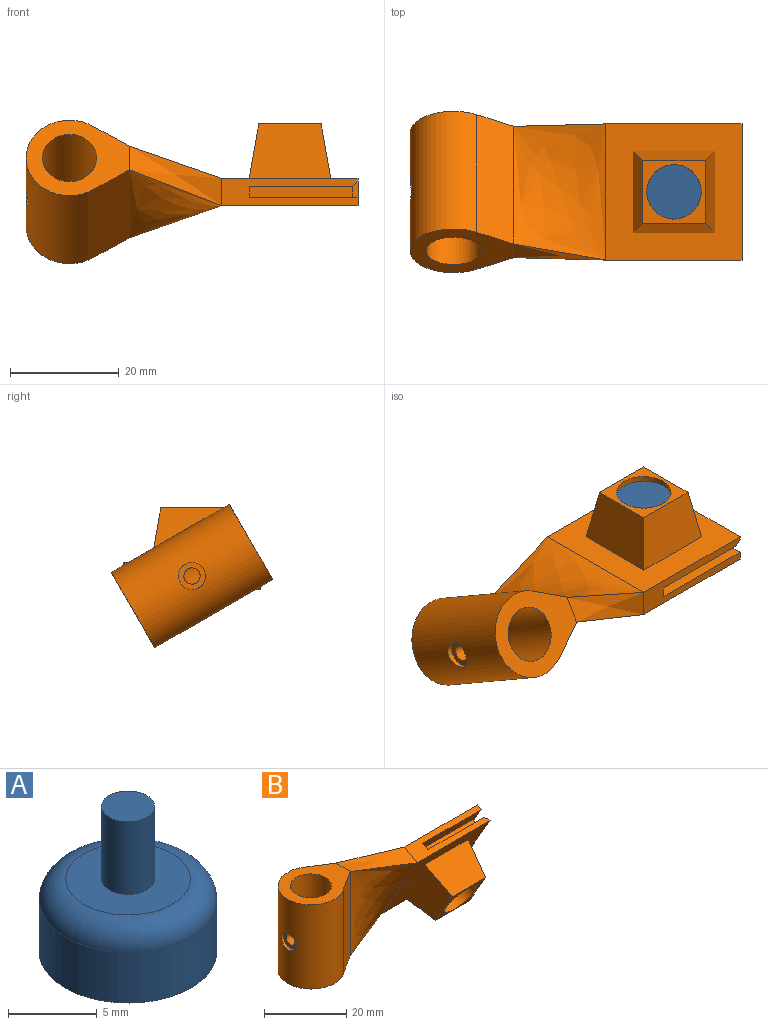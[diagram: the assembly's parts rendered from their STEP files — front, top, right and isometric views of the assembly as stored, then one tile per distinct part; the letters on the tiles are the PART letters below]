
ASSEMBLY  parts=2 mates=1
PART A: 6 faces, bbox 10.8x10.8x10 mm
  f0: cylinder r=5mm len=10mm, axis (0,0,-1), area 110mm2, adj f2,f3
  f1: plane 7x7mm, normal (0,0,1), area 31.4mm2, adj f3,f4
  f2: plane 10x10mm, normal (0,0,-1), area 78.5mm2, adj f0
  f3: torus R=3.5mm, axis (0,0,1), area 66mm2, adj f0,f1
  f4: cylinder r=1.5mm len=5mm, axis (0,0,-1), area 47.1mm2, adj f1,f5
  f5: plane 3x3mm, normal (0,0,1), area 7.1mm2, adj f4
PART B: 38 faces, bbox 61x22.1x25 mm
  f0: plane 24.15x16.83mm, normal (1,0,0), area 95mm2, adj f14,f15,f16,f17,f25,f28,f31,f32
  f1: cylinder r=8mm len=25mm, axis (0,0,-1), area 834.4mm2, adj f3,f4,f5,f6,f8
  f2: cylinder r=5mm len=25mm, axis (0,0,-1), area 778.2mm2, adj f5,f6,f7
  f3: plane 25x6.72mm, normal (0.54,0.84,0), area 198.8mm2, adj f1,f5,f6,f10
  f4: plane 25x6.72mm, normal (0.54,-0.84,0), area 198.8mm2, adj f1,f5,f6,f12
  f5: plane 19x16mm, normal (0,0,1), area 149.3mm2, adj f1,f2,f3,f4,f11
  f6: plane 19x16mm, normal (0,0,-1), area 149.3mm2, adj f1,f2,f3,f4,f13
  f7: cylinder r=1.5mm len=3mm, axis (-1,0,0), area 19.9mm2, adj f2,f9
  f8: cylinder r=2.5mm len=5mm, axis (-1,0,0), area 12.6mm2, adj f1,f9
  f9: plane 5x5mm, normal (-1,0,0), area 12.6mm2, adj f7,f8
  f10: bspline ~25x17mm, area 425mm2, adj f3,f11,f13,f15
  f11: bspline ~17x10.92mm, area 83.3mm2, adj f5,f10,f12,f16
  f12: bspline ~25x17mm, area 425mm2, adj f4,f11,f13,f17
  f13: bspline ~17x10.92mm, area 83.3mm2, adj f6,f10,f12,f14
  f14: plane 25x4.33mm, normal (0,0.5,-0.87), area 84.5mm2, adj f0,f13,f15,f17,f27,f28,f30,f33
  f15: plane 25x21.65mm, normal (0,0.87,0.5), area 617.9mm2, adj f0,f10,f14,f16,f37
  f16: plane 25x4.33mm, normal (0,-0.5,0.87), area 84.5mm2, adj f0,f11,f15,f17,f23,f25,f26,f32
  f17: plane 25x21.65mm, normal (0,-0.87,-0.5), area 400mm2, adj f0,f12,f14,f16,f18,f19,f20,f21
  f18: plane 16.46x15.28mm, normal (0.98,-0.15,-0.09), area 134.4mm2, adj f17,f19,f21,f22
  f19: plane 15x7.78mm, normal (0,-0.64,0.77), area 134.4mm2, adj f17,f18,f20,f22
  f20: plane 16.46x15.28mm, normal (-0.98,-0.15,-0.09), area 134.4mm2, adj f17,f19,f21,f22
  f21: plane 15x9.54mm, normal (0,0.34,-0.94), area 134.4mm2, adj f17,f18,f20,f22
  f22: plane 11.47x9.94mm, normal (0,-0.87,-0.5), area 53.1mm2, adj f18,f19,f20,f21,f35
  f23: plane 19x3.46mm, normal (0,0.87,0.5), area 76mm2, adj f16,f24,f26,f32
  f24: plane 19x1.73mm, normal (0,-0.5,0.87), area 38mm2, adj f23,f25,f26,f31
  f25: plane 20x4.33mm, normal (0,-0.87,-0.5), area 80.5mm2, adj f0,f16,f24,f26,f31
  f26: plane 4.46x3.73mm, normal (1,0,0), area 8mm2, adj f16,f23,f24,f25
  f27: plane 19x3.46mm, normal (0,0.87,0.5), area 76mm2, adj f14,f29,f30,f33
  f28: plane 20x4.33mm, normal (0,-0.87,-0.5), area 80.5mm2, adj f0,f14,f29,f30,f34
  f29: plane 19x1.73mm, normal (0,0.5,-0.87), area 38mm2, adj f27,f28,f30,f34
  f30: plane 4.46x3.73mm, normal (1,0,0), area 8mm2, adj f14,f27,f28,f29
  f31: plane 2.6x2.37mm, normal (0.71,-0.35,0.61), area 3.5mm2, adj f0,f24,f25,f32
  f32: plane 4.83x2.87mm, normal (0.71,0.61,0.35), area 6.4mm2, adj f0,f16,f23,f31
  f33: plane 4.33x3.37mm, normal (0.71,0.61,0.35), area 6.4mm2, adj f0,f14,f27,f34
  f34: plane 3.1x1.87mm, normal (0.71,0.35,-0.61), area 3.5mm2, adj f0,f28,f29,f33
  f35: cylinder r=5mm len=11.66mm, axis (0,-0.87,-0.5), area 188.5mm2, adj f22,f36
  f36: plane 10x8.66mm, normal (0,-0.87,-0.5), area 71.5mm2, adj f35,f37
  f37: cylinder r=1.5mm len=9.29mm, axis (0,-0.87,-0.5), area 84.8mm2, adj f15,f36
PLACE A rot(axis=(1,0,0),180deg) t=(0,0,9)mm
PLACE B rot(axis=(-1,0,0),120deg) t=(-40.5,-10.83,3.75)mm
MATE fastened A.f0 <-> B.f35  axis (0,0,-1) through (0,0,4)mm
